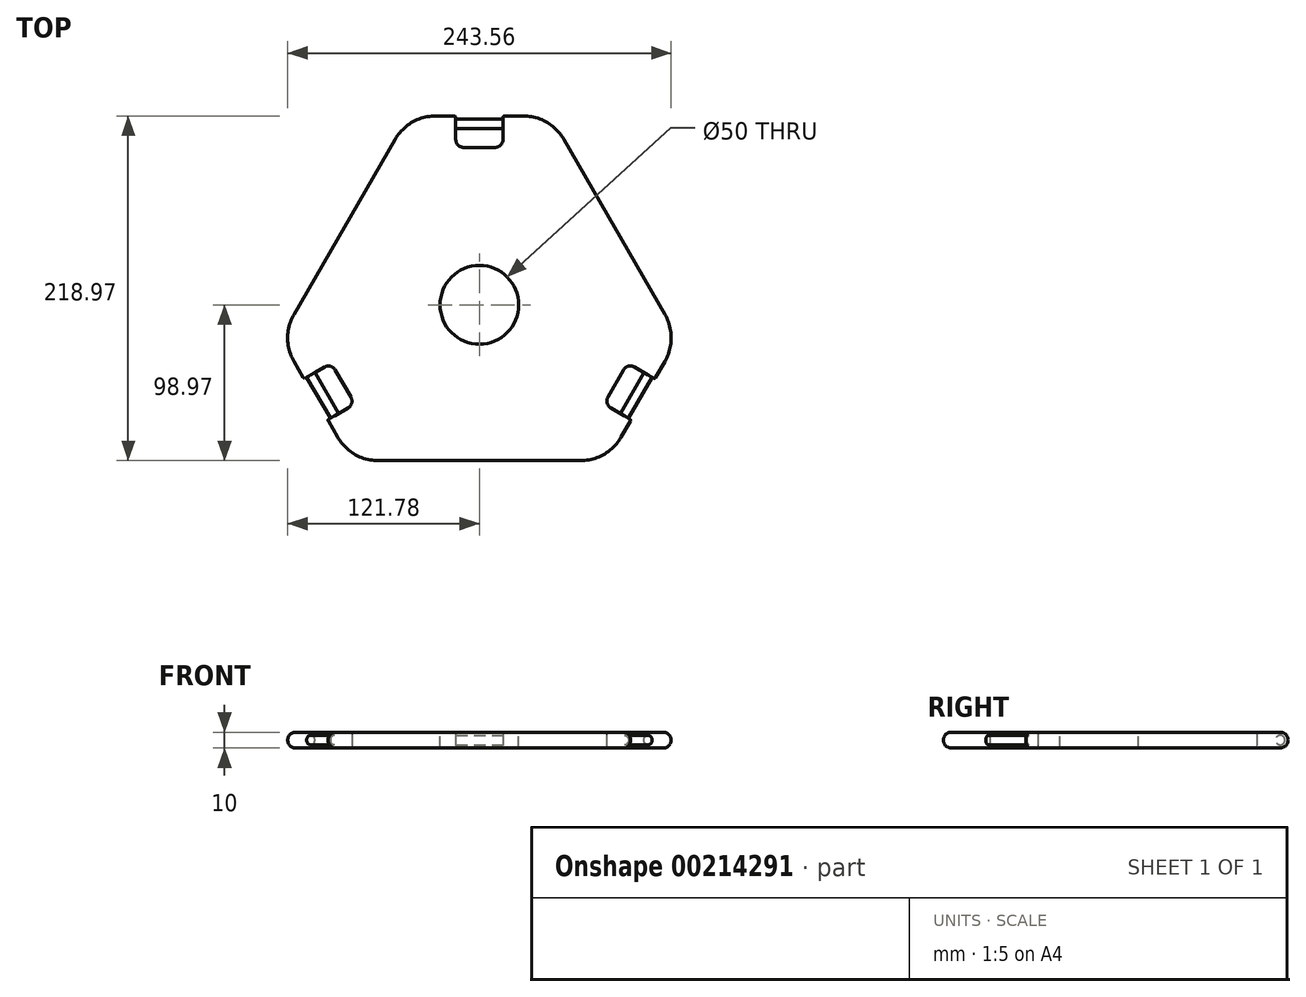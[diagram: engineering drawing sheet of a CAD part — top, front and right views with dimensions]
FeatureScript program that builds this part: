
annotation { "Feature Type Name" : "Feature", "Feature Type Description" : "" }
export const myFeature = defineFeature(function(context is Context, id is Id, definition is map)
    precondition{}
    {
        {
            var Q0;
            Q0=qCreatedBy(makeId("Top.planeOp"),FACE);
            var sketch = newSketch(context, id + "F0", { "sketchPlane" : qUnion([Q0])});
            skLineSegment(sketch, "E0", {"start": v(0, 100) * mm, "end": v(15, 100) * mm});
            skLineSegment(sketch, "E1", {"start": v(15, 100) * mm, "end": v(15, 120) * mm});
            skLineSegment(sketch, "E2", {"start": v(0, 0) * mm, "end": v(0, 100) * mm, "construction": true});
            skLineSegment(sketch, "E3.MirrorCS", {"start": v(0, 100) * mm, "end": v(-15, 100) * mm});
            skLineSegment(sketch, "E4.MirrorCS", {"start": v(-15, 100) * mm, "end": v(-15, 120) * mm});
            skLineSegment(sketch, "E5.1.0", {"start": v(-79.1, -63) * mm, "end": v(-96.42, -73) * mm});
            skLineSegment(sketch, "E5.1.1", {"start": v(-86.6, -50) * mm, "end": v(-79.1, -63) * mm});
            skLineSegment(sketch, "E5.1.2", {"start": v(-86.6, -50) * mm, "end": v(-94.1, -37) * mm});
            skLineSegment(sketch, "E5.1.3", {"start": v(-94.1, -37) * mm, "end": v(-111.42, -47) * mm});
            skLineSegment(sketch, "E5.2.0", {"start": v(94.1, -37) * mm, "end": v(111.42, -47) * mm});
            skLineSegment(sketch, "E5.2.1", {"start": v(86.6, -50) * mm, "end": v(94.1, -37) * mm});
            skLineSegment(sketch, "E5.2.2", {"start": v(86.6, -50) * mm, "end": v(79.1, -63) * mm});
            skLineSegment(sketch, "E5.2.3", {"start": v(79.1, -63) * mm, "end": v(96.42, -73) * mm});
            skPoint(sketch, "E5.center", {"position": v(0, 0) * mm});
            skLineSegment(sketch, "E6", {"start": v(15, 120) * mm, "end": v(45, 120) * mm});
            skLineSegment(sketch, "E7", {"start": v(45, 120) * mm, "end": v(126.42, -21.03) * mm});
            skLineSegment(sketch, "E8", {"start": v(126.42, -21.03) * mm, "end": v(111.42, -47) * mm});
            skLineSegment(sketch, "E9.1.0", {"start": v(-111.42, -47) * mm, "end": v(-126.42, -21.03) * mm});
            skLineSegment(sketch, "E9.1.1", {"start": v(-126.42, -21.03) * mm, "end": v(-45, 120) * mm});
            skLineSegment(sketch, "E9.1.2", {"start": v(-45, 120) * mm, "end": v(-15, 120) * mm});
            skLineSegment(sketch, "E9.2.0", {"start": v(96.42, -73) * mm, "end": v(81.42, -98.97) * mm});
            skLineSegment(sketch, "E9.2.1", {"start": v(81.42, -98.97) * mm, "end": v(-81.42, -98.97) * mm});
            skLineSegment(sketch, "E9.2.2", {"start": v(-81.42, -98.97) * mm, "end": v(-96.42, -73) * mm});
            skSolve(sketch);
        }
        {
            var Q0;
            Q0 = qSketchRegion(id + "F0", true);
            extrude(context, id + "F1", {"entities" : qUnion([Q0]), "depth" : 10 * mm});
        }
        {
            var Q0;
            Q0=makeQuery(id+"F1.opExtrude","SWEPT_EDGE",EDGE,{"disambiguationData":[OSD([sQuery(id+"F0.wireOp",EDGE,"E9.1.1"),sQuery(id+"F0.wireOp",EDGE,"E9.1.2")])]});
            var Q1;
            Q1=makeQuery(id+"F1.opExtrude","SWEPT_EDGE",EDGE,{"disambiguationData":[OSD([sQuery(id+"F0.wireOp",EDGE,"E6"),sQuery(id+"F0.wireOp",EDGE,"E7")])]});
            var Q2;
            Q2=makeQuery(id+"F1.opExtrude","SWEPT_EDGE",EDGE,{"disambiguationData":[OSD([sQuery(id+"F0.wireOp",EDGE,"E9.1.0"),sQuery(id+"F0.wireOp",EDGE,"E9.1.1")])]});
            var Q3;
            Q3=makeQuery(id+"F1.opExtrude","SWEPT_EDGE",EDGE,{"disambiguationData":[OSD([sQuery(id+"F0.wireOp",EDGE,"E7"),sQuery(id+"F0.wireOp",EDGE,"E8")])]});
            var Q4;
            Q4=makeQuery(id+"F1.opExtrude","SWEPT_EDGE",EDGE,{"disambiguationData":[OSD([sQuery(id+"F0.wireOp",EDGE,"E9.2.0"),sQuery(id+"F0.wireOp",EDGE,"E9.2.1")])]});
            var Q5;
            Q5=makeQuery(id+"F1.opExtrude","SWEPT_EDGE",EDGE,{"disambiguationData":[OSD([sQuery(id+"F0.wireOp",EDGE,"E9.2.1"),sQuery(id+"F0.wireOp",EDGE,"E9.2.2")])]});
            fillet(context, id + "F2", {"entities" : qUnion([Q0, Q1, Q2, Q3, Q4, Q5]), "radius" : 30 * mm, "tangentPropagation" : true, "allowEdgeOverflow" : false});
        }
        {
            var Q0;
            {var subQ0=sQuery(id+"F0.wireOp",EDGE,"E7");var subQ1=sQuery(id+"F0.wireOp",EDGE,"E6");Q0=makeQuery(id+"F2.opFillet","BLEND_EDGE",EDGE,{"blendedFrom":[makeQuery(id+"F1.opExtrude","SWEPT_EDGE",EDGE,{"disambiguationData":[OSD([subQ1,subQ0])]}),makeQuery(id+"F1.opExtrude","CAP_FACE",FACE,{"disambiguationData":[OSD([sQuery(id+"F0.wireOp",EDGE,"E0"),sQuery(id+"F0.wireOp",EDGE,"E1"),sQuery(id+"F0.wireOp",EDGE,"E3.MirrorCS"),sQuery(id+"F0.wireOp",EDGE,"E4.MirrorCS"),sQuery(id+"F0.wireOp",EDGE,"E5.1.0"),sQuery(id+"F0.wireOp",EDGE,"E5.1.1"),sQuery(id+"F0.wireOp",EDGE,"E5.1.2"),sQuery(id+"F0.wireOp",EDGE,"E5.1.3"),sQuery(id+"F0.wireOp",EDGE,"E5.2.0"),sQuery(id+"F0.wireOp",EDGE,"E5.2.1"),sQuery(id+"F0.wireOp",EDGE,"E5.2.2"),sQuery(id+"F0.wireOp",EDGE,"E5.2.3"),subQ1,subQ0,sQuery(id+"F0.wireOp",EDGE,"E8"),sQuery(id+"F0.wireOp",EDGE,"E9.1.0"),sQuery(id+"F0.wireOp",EDGE,"E9.1.1"),sQuery(id+"F0.wireOp",EDGE,"E9.1.2"),sQuery(id+"F0.wireOp",EDGE,"E9.2.0"),sQuery(id+"F0.wireOp",EDGE,"E9.2.1"),sQuery(id+"F0.wireOp",EDGE,"E9.2.2")])],"isStart":false})],"blendedInto":[makeQuery(id+"F1.opExtrude","CAP_FACE",FACE,{"disambiguationData":[OSD([sQuery(id+"F0.wireOp",EDGE,"E0"),sQuery(id+"F0.wireOp",EDGE,"E1"),sQuery(id+"F0.wireOp",EDGE,"E3.MirrorCS"),sQuery(id+"F0.wireOp",EDGE,"E4.MirrorCS"),sQuery(id+"F0.wireOp",EDGE,"E5.1.0"),sQuery(id+"F0.wireOp",EDGE,"E5.1.1"),sQuery(id+"F0.wireOp",EDGE,"E5.1.2"),sQuery(id+"F0.wireOp",EDGE,"E5.1.3"),sQuery(id+"F0.wireOp",EDGE,"E5.2.0"),sQuery(id+"F0.wireOp",EDGE,"E5.2.1"),sQuery(id+"F0.wireOp",EDGE,"E5.2.2"),sQuery(id+"F0.wireOp",EDGE,"E5.2.3"),subQ1,subQ0,sQuery(id+"F0.wireOp",EDGE,"E8"),sQuery(id+"F0.wireOp",EDGE,"E9.1.0"),sQuery(id+"F0.wireOp",EDGE,"E9.1.1"),sQuery(id+"F0.wireOp",EDGE,"E9.1.2"),sQuery(id+"F0.wireOp",EDGE,"E9.2.0"),sQuery(id+"F0.wireOp",EDGE,"E9.2.1"),sQuery(id+"F0.wireOp",EDGE,"E9.2.2")])],"isStart":false})]});}
            var Q1;
            {var subQ0=sQuery(id+"F0.wireOp",EDGE,"E9.2.1");var subQ1=sQuery(id+"F0.wireOp",EDGE,"E9.2.0");Q1=makeQuery(id+"F2.opFillet","BLEND_EDGE",EDGE,{"blendedFrom":[makeQuery(id+"F1.opExtrude","SWEPT_EDGE",EDGE,{"disambiguationData":[OSD([subQ1,subQ0])]}),makeQuery(id+"F1.opExtrude","CAP_FACE",FACE,{"disambiguationData":[OSD([sQuery(id+"F0.wireOp",EDGE,"E0"),sQuery(id+"F0.wireOp",EDGE,"E1"),sQuery(id+"F0.wireOp",EDGE,"E3.MirrorCS"),sQuery(id+"F0.wireOp",EDGE,"E4.MirrorCS"),sQuery(id+"F0.wireOp",EDGE,"E5.1.0"),sQuery(id+"F0.wireOp",EDGE,"E5.1.1"),sQuery(id+"F0.wireOp",EDGE,"E5.1.2"),sQuery(id+"F0.wireOp",EDGE,"E5.1.3"),sQuery(id+"F0.wireOp",EDGE,"E5.2.0"),sQuery(id+"F0.wireOp",EDGE,"E5.2.1"),sQuery(id+"F0.wireOp",EDGE,"E5.2.2"),sQuery(id+"F0.wireOp",EDGE,"E5.2.3"),sQuery(id+"F0.wireOp",EDGE,"E6"),sQuery(id+"F0.wireOp",EDGE,"E7"),sQuery(id+"F0.wireOp",EDGE,"E8"),sQuery(id+"F0.wireOp",EDGE,"E9.1.0"),sQuery(id+"F0.wireOp",EDGE,"E9.1.1"),sQuery(id+"F0.wireOp",EDGE,"E9.1.2"),subQ1,subQ0,sQuery(id+"F0.wireOp",EDGE,"E9.2.2")])],"isStart":false})],"blendedInto":[makeQuery(id+"F1.opExtrude","CAP_FACE",FACE,{"disambiguationData":[OSD([sQuery(id+"F0.wireOp",EDGE,"E0"),sQuery(id+"F0.wireOp",EDGE,"E1"),sQuery(id+"F0.wireOp",EDGE,"E3.MirrorCS"),sQuery(id+"F0.wireOp",EDGE,"E4.MirrorCS"),sQuery(id+"F0.wireOp",EDGE,"E5.1.0"),sQuery(id+"F0.wireOp",EDGE,"E5.1.1"),sQuery(id+"F0.wireOp",EDGE,"E5.1.2"),sQuery(id+"F0.wireOp",EDGE,"E5.1.3"),sQuery(id+"F0.wireOp",EDGE,"E5.2.0"),sQuery(id+"F0.wireOp",EDGE,"E5.2.1"),sQuery(id+"F0.wireOp",EDGE,"E5.2.2"),sQuery(id+"F0.wireOp",EDGE,"E5.2.3"),sQuery(id+"F0.wireOp",EDGE,"E6"),sQuery(id+"F0.wireOp",EDGE,"E7"),sQuery(id+"F0.wireOp",EDGE,"E8"),sQuery(id+"F0.wireOp",EDGE,"E9.1.0"),sQuery(id+"F0.wireOp",EDGE,"E9.1.1"),sQuery(id+"F0.wireOp",EDGE,"E9.1.2"),subQ1,subQ0,sQuery(id+"F0.wireOp",EDGE,"E9.2.2")])],"isStart":false})]});}
            var Q2;
            Q2=makeQuery(id+"F1.opExtrude","CAP_EDGE",EDGE,{"disambiguationData":[OSD([sQuery(id+"F0.wireOp",EDGE,"E9.1.1")])],"isStart":false});
            var Q3;
            {var subQ0=sQuery(id+"F0.wireOp",EDGE,"E9.2.1");var subQ1=sQuery(id+"F0.wireOp",EDGE,"E9.2.0");Q3=makeQuery(id+"F2.opFillet","BLEND_EDGE",EDGE,{"blendedFrom":[makeQuery(id+"F1.opExtrude","SWEPT_EDGE",EDGE,{"disambiguationData":[OSD([subQ1,subQ0])]}),makeQuery(id+"F1.opExtrude","CAP_FACE",FACE,{"disambiguationData":[OSD([sQuery(id+"F0.wireOp",EDGE,"E0"),sQuery(id+"F0.wireOp",EDGE,"E1"),sQuery(id+"F0.wireOp",EDGE,"E3.MirrorCS"),sQuery(id+"F0.wireOp",EDGE,"E4.MirrorCS"),sQuery(id+"F0.wireOp",EDGE,"E5.1.0"),sQuery(id+"F0.wireOp",EDGE,"E5.1.1"),sQuery(id+"F0.wireOp",EDGE,"E5.1.2"),sQuery(id+"F0.wireOp",EDGE,"E5.1.3"),sQuery(id+"F0.wireOp",EDGE,"E5.2.0"),sQuery(id+"F0.wireOp",EDGE,"E5.2.1"),sQuery(id+"F0.wireOp",EDGE,"E5.2.2"),sQuery(id+"F0.wireOp",EDGE,"E5.2.3"),sQuery(id+"F0.wireOp",EDGE,"E6"),sQuery(id+"F0.wireOp",EDGE,"E7"),sQuery(id+"F0.wireOp",EDGE,"E8"),sQuery(id+"F0.wireOp",EDGE,"E9.1.0"),sQuery(id+"F0.wireOp",EDGE,"E9.1.1"),sQuery(id+"F0.wireOp",EDGE,"E9.1.2"),subQ1,subQ0,sQuery(id+"F0.wireOp",EDGE,"E9.2.2")])],"isStart":true})],"blendedInto":[makeQuery(id+"F1.opExtrude","CAP_FACE",FACE,{"disambiguationData":[OSD([sQuery(id+"F0.wireOp",EDGE,"E0"),sQuery(id+"F0.wireOp",EDGE,"E1"),sQuery(id+"F0.wireOp",EDGE,"E3.MirrorCS"),sQuery(id+"F0.wireOp",EDGE,"E4.MirrorCS"),sQuery(id+"F0.wireOp",EDGE,"E5.1.0"),sQuery(id+"F0.wireOp",EDGE,"E5.1.1"),sQuery(id+"F0.wireOp",EDGE,"E5.1.2"),sQuery(id+"F0.wireOp",EDGE,"E5.1.3"),sQuery(id+"F0.wireOp",EDGE,"E5.2.0"),sQuery(id+"F0.wireOp",EDGE,"E5.2.1"),sQuery(id+"F0.wireOp",EDGE,"E5.2.2"),sQuery(id+"F0.wireOp",EDGE,"E5.2.3"),sQuery(id+"F0.wireOp",EDGE,"E6"),sQuery(id+"F0.wireOp",EDGE,"E7"),sQuery(id+"F0.wireOp",EDGE,"E8"),sQuery(id+"F0.wireOp",EDGE,"E9.1.0"),sQuery(id+"F0.wireOp",EDGE,"E9.1.1"),sQuery(id+"F0.wireOp",EDGE,"E9.1.2"),subQ1,subQ0,sQuery(id+"F0.wireOp",EDGE,"E9.2.2")])],"isStart":true})]});}
            var Q4;
            {var subQ0=sQuery(id+"F0.wireOp",EDGE,"E8");var subQ1=sQuery(id+"F0.wireOp",EDGE,"E7");Q4=makeQuery(id+"F2.opFillet","BLEND_EDGE",EDGE,{"blendedFrom":[makeQuery(id+"F1.opExtrude","SWEPT_EDGE",EDGE,{"disambiguationData":[OSD([subQ1,subQ0])]}),makeQuery(id+"F1.opExtrude","CAP_FACE",FACE,{"disambiguationData":[OSD([sQuery(id+"F0.wireOp",EDGE,"E0"),sQuery(id+"F0.wireOp",EDGE,"E1"),sQuery(id+"F0.wireOp",EDGE,"E3.MirrorCS"),sQuery(id+"F0.wireOp",EDGE,"E4.MirrorCS"),sQuery(id+"F0.wireOp",EDGE,"E5.1.0"),sQuery(id+"F0.wireOp",EDGE,"E5.1.1"),sQuery(id+"F0.wireOp",EDGE,"E5.1.2"),sQuery(id+"F0.wireOp",EDGE,"E5.1.3"),sQuery(id+"F0.wireOp",EDGE,"E5.2.0"),sQuery(id+"F0.wireOp",EDGE,"E5.2.1"),sQuery(id+"F0.wireOp",EDGE,"E5.2.2"),sQuery(id+"F0.wireOp",EDGE,"E5.2.3"),sQuery(id+"F0.wireOp",EDGE,"E6"),subQ1,subQ0,sQuery(id+"F0.wireOp",EDGE,"E9.1.0"),sQuery(id+"F0.wireOp",EDGE,"E9.1.1"),sQuery(id+"F0.wireOp",EDGE,"E9.1.2"),sQuery(id+"F0.wireOp",EDGE,"E9.2.0"),sQuery(id+"F0.wireOp",EDGE,"E9.2.1"),sQuery(id+"F0.wireOp",EDGE,"E9.2.2")])],"isStart":true})],"blendedInto":[makeQuery(id+"F1.opExtrude","CAP_FACE",FACE,{"disambiguationData":[OSD([sQuery(id+"F0.wireOp",EDGE,"E0"),sQuery(id+"F0.wireOp",EDGE,"E1"),sQuery(id+"F0.wireOp",EDGE,"E3.MirrorCS"),sQuery(id+"F0.wireOp",EDGE,"E4.MirrorCS"),sQuery(id+"F0.wireOp",EDGE,"E5.1.0"),sQuery(id+"F0.wireOp",EDGE,"E5.1.1"),sQuery(id+"F0.wireOp",EDGE,"E5.1.2"),sQuery(id+"F0.wireOp",EDGE,"E5.1.3"),sQuery(id+"F0.wireOp",EDGE,"E5.2.0"),sQuery(id+"F0.wireOp",EDGE,"E5.2.1"),sQuery(id+"F0.wireOp",EDGE,"E5.2.2"),sQuery(id+"F0.wireOp",EDGE,"E5.2.3"),sQuery(id+"F0.wireOp",EDGE,"E6"),subQ1,subQ0,sQuery(id+"F0.wireOp",EDGE,"E9.1.0"),sQuery(id+"F0.wireOp",EDGE,"E9.1.1"),sQuery(id+"F0.wireOp",EDGE,"E9.1.2"),sQuery(id+"F0.wireOp",EDGE,"E9.2.0"),sQuery(id+"F0.wireOp",EDGE,"E9.2.1"),sQuery(id+"F0.wireOp",EDGE,"E9.2.2")])],"isStart":true})]});}
            var Q5;
            {var subQ0=sQuery(id+"F0.wireOp",EDGE,"E9.1.1");var subQ1=sQuery(id+"F0.wireOp",EDGE,"E9.1.0");Q5=makeQuery(id+"F2.opFillet","BLEND_EDGE",EDGE,{"blendedFrom":[makeQuery(id+"F1.opExtrude","SWEPT_EDGE",EDGE,{"disambiguationData":[OSD([subQ1,subQ0])]}),makeQuery(id+"F1.opExtrude","CAP_FACE",FACE,{"disambiguationData":[OSD([sQuery(id+"F0.wireOp",EDGE,"E0"),sQuery(id+"F0.wireOp",EDGE,"E1"),sQuery(id+"F0.wireOp",EDGE,"E3.MirrorCS"),sQuery(id+"F0.wireOp",EDGE,"E4.MirrorCS"),sQuery(id+"F0.wireOp",EDGE,"E5.1.0"),sQuery(id+"F0.wireOp",EDGE,"E5.1.1"),sQuery(id+"F0.wireOp",EDGE,"E5.1.2"),sQuery(id+"F0.wireOp",EDGE,"E5.1.3"),sQuery(id+"F0.wireOp",EDGE,"E5.2.0"),sQuery(id+"F0.wireOp",EDGE,"E5.2.1"),sQuery(id+"F0.wireOp",EDGE,"E5.2.2"),sQuery(id+"F0.wireOp",EDGE,"E5.2.3"),sQuery(id+"F0.wireOp",EDGE,"E6"),sQuery(id+"F0.wireOp",EDGE,"E7"),sQuery(id+"F0.wireOp",EDGE,"E8"),subQ1,subQ0,sQuery(id+"F0.wireOp",EDGE,"E9.1.2"),sQuery(id+"F0.wireOp",EDGE,"E9.2.0"),sQuery(id+"F0.wireOp",EDGE,"E9.2.1"),sQuery(id+"F0.wireOp",EDGE,"E9.2.2")])],"isStart":true})],"blendedInto":[makeQuery(id+"F1.opExtrude","CAP_FACE",FACE,{"disambiguationData":[OSD([sQuery(id+"F0.wireOp",EDGE,"E0"),sQuery(id+"F0.wireOp",EDGE,"E1"),sQuery(id+"F0.wireOp",EDGE,"E3.MirrorCS"),sQuery(id+"F0.wireOp",EDGE,"E4.MirrorCS"),sQuery(id+"F0.wireOp",EDGE,"E5.1.0"),sQuery(id+"F0.wireOp",EDGE,"E5.1.1"),sQuery(id+"F0.wireOp",EDGE,"E5.1.2"),sQuery(id+"F0.wireOp",EDGE,"E5.1.3"),sQuery(id+"F0.wireOp",EDGE,"E5.2.0"),sQuery(id+"F0.wireOp",EDGE,"E5.2.1"),sQuery(id+"F0.wireOp",EDGE,"E5.2.2"),sQuery(id+"F0.wireOp",EDGE,"E5.2.3"),sQuery(id+"F0.wireOp",EDGE,"E6"),sQuery(id+"F0.wireOp",EDGE,"E7"),sQuery(id+"F0.wireOp",EDGE,"E8"),subQ1,subQ0,sQuery(id+"F0.wireOp",EDGE,"E9.1.2"),sQuery(id+"F0.wireOp",EDGE,"E9.2.0"),sQuery(id+"F0.wireOp",EDGE,"E9.2.1"),sQuery(id+"F0.wireOp",EDGE,"E9.2.2")])],"isStart":true})]});}
            fillet(context, id + "F3", {"entities" : qUnion([Q0, Q1, Q2, Q3, Q4, Q5]), "radius" : 5 * mm, "tangentPropagation" : true, "allowEdgeOverflow" : false});
        }
        {
            var Q0;
            Q0=qCreatedBy(makeId("Right.planeOp"),FACE);
            var sketch = newSketch(context, id + "F4", { "sketchPlane" : qUnion([Q0])});
            skLineSegment(sketch, "E10", {"start": v(0, 0) * mm, "end": v(0, 47.73) * mm});
            skSolve(sketch);
        }
        {
            var Q0;
            Q0=makeQuery(id+"F1.opExtrude","SWEPT_FACE",FACE,{"disambiguationData":[OSD([sQuery(id+"F0.wireOp",EDGE,"E1")])]});
            var sketch = newSketch(context, id + "F5", { "sketchPlane" : qUnion([Q0])});
            skCircle(sketch, "E11", {"center": v(-115, 5) * mm, "radius": 3 * mm});
            skSolve(sketch);
        }
        {
            var Q0;
            Q0 = qSketchRegion(id + "F5", true);
            var Q1;
            Q1=makeQuery(id+"F1.opExtrude","SWEPT_FACE",FACE,{"disambiguationData":[OSD([sQuery(id+"F0.wireOp",EDGE,"E4.MirrorCS")])]});
            extrude(context, id + "F6", {"entities" : qUnion([Q0]), "endBound" : BoundingType.UP_TO_SURFACE, "endBoundEntityFace" : qUnion([Q1]), "depth" : 25 * mm});
        }
        {
            var Q0;
            Q0=makeQuery(id+"F6.opExtrude","SWEPT_BODY",BODY,{"disambiguationData":[OSD([sQuery(id+"F5.wireOp",EDGE,"E11")])]});
            var Q1;
            Q1=sQuery(id+"F4.wireOp",EDGE,"E10");
            circularPattern(context, id + "F7", {"entities" : qUnion([Q0]), "axis" : qUnion([Q1]), "angle" : 360 * degree, "instanceCount" : 3, "equalSpace" : true});
        }
        {
            var Q0;
            Q0=makeQuery(id+"F1.opExtrude","SWEPT_EDGE",EDGE,{"disambiguationData":[OSD([sQuery(id+"F0.wireOp",EDGE,"E5.1.0"),sQuery(id+"F0.wireOp",EDGE,"E5.1.1")])]});
            var Q1;
            Q1=makeQuery(id+"F1.opExtrude","SWEPT_EDGE",EDGE,{"disambiguationData":[OSD([sQuery(id+"F0.wireOp",EDGE,"E5.1.2"),sQuery(id+"F0.wireOp",EDGE,"E5.1.3")])]});
            var Q2;
            Q2=makeQuery(id+"F1.opExtrude","SWEPT_EDGE",EDGE,{"disambiguationData":[OSD([sQuery(id+"F0.wireOp",EDGE,"E5.2.0"),sQuery(id+"F0.wireOp",EDGE,"E5.2.1")])]});
            var Q3;
            Q3=makeQuery(id+"F1.opExtrude","SWEPT_EDGE",EDGE,{"disambiguationData":[OSD([sQuery(id+"F0.wireOp",EDGE,"E5.2.2"),sQuery(id+"F0.wireOp",EDGE,"E5.2.3")])]});
            var Q4;
            Q4=makeQuery(id+"F1.opExtrude","SWEPT_EDGE",EDGE,{"disambiguationData":[OSD([sQuery(id+"F0.wireOp",EDGE,"E3.MirrorCS"),sQuery(id+"F0.wireOp",EDGE,"E4.MirrorCS")])]});
            var Q5;
            Q5=makeQuery(id+"F1.opExtrude","SWEPT_EDGE",EDGE,{"disambiguationData":[OSD([sQuery(id+"F0.wireOp",EDGE,"E0"),sQuery(id+"F0.wireOp",EDGE,"E1")])]});
            fillet(context, id + "F8", {"entities" : qUnion([Q0, Q1, Q2, Q3, Q4, Q5]), "radius" : 5 * mm, "tangentPropagation" : true, "allowEdgeOverflow" : false});
        }
        {
            var Q0;
            Q0=makeQuery(id+"F1.opExtrude","CAP_EDGE",EDGE,{"disambiguationData":[OSD([sQuery(id+"F0.wireOp",EDGE,"E5.1.3")])],"isStart":true});
            var Q1;
            Q1=makeQuery(id+"F1.opExtrude","CAP_EDGE",EDGE,{"disambiguationData":[OSD([sQuery(id+"F0.wireOp",EDGE,"E4.MirrorCS")])],"isStart":true});
            var Q2;
            Q2=makeQuery(id+"F1.opExtrude","CAP_EDGE",EDGE,{"disambiguationData":[OSD([sQuery(id+"F0.wireOp",EDGE,"E5.2.1"),sQuery(id+"F0.wireOp",EDGE,"E5.2.2")])],"isStart":true});
            fillet(context, id + "F9", {"entities" : qUnion([Q0, Q1, Q2]), "radius" : 1 * mm, "tangentPropagation" : true, "allowEdgeOverflow" : false});
        }
        {
            var Q0;
            Q0=makeQuery(id+"F1.opExtrude","CAP_FACE",FACE,{"disambiguationData":[OSD([sQuery(id+"F0.wireOp",EDGE,"E0"),sQuery(id+"F0.wireOp",EDGE,"E1"),sQuery(id+"F0.wireOp",EDGE,"E3.MirrorCS"),sQuery(id+"F0.wireOp",EDGE,"E4.MirrorCS"),sQuery(id+"F0.wireOp",EDGE,"E5.1.0"),sQuery(id+"F0.wireOp",EDGE,"E5.1.1"),sQuery(id+"F0.wireOp",EDGE,"E5.1.2"),sQuery(id+"F0.wireOp",EDGE,"E5.1.3"),sQuery(id+"F0.wireOp",EDGE,"E5.2.0"),sQuery(id+"F0.wireOp",EDGE,"E5.2.1"),sQuery(id+"F0.wireOp",EDGE,"E5.2.2"),sQuery(id+"F0.wireOp",EDGE,"E5.2.3"),sQuery(id+"F0.wireOp",EDGE,"E6"),sQuery(id+"F0.wireOp",EDGE,"E7"),sQuery(id+"F0.wireOp",EDGE,"E8"),sQuery(id+"F0.wireOp",EDGE,"E9.1.0"),sQuery(id+"F0.wireOp",EDGE,"E9.1.1"),sQuery(id+"F0.wireOp",EDGE,"E9.1.2"),sQuery(id+"F0.wireOp",EDGE,"E9.2.0"),sQuery(id+"F0.wireOp",EDGE,"E9.2.1"),sQuery(id+"F0.wireOp",EDGE,"E9.2.2")])],"isStart":false});
            var sketch = newSketch(context, id + "F10", { "sketchPlane" : qUnion([Q0])});
            skCircle(sketch, "E12", {"center": v(0, 0) * mm, "radius": 25 * mm});
            skSolve(sketch);
        }
        {
            var Q0;
            Q0=makeQuery(id+"F10.imprint","IMPRINT",FACE,{"disambiguationData":[TD([[makeQuery(id+"F10.imprint","IMPRINT",EDGE,{"derivedFrom":sQuery(id+"F10.wireOp",EDGE,"E12")}),1.0]])]});
            extrude(context, id + "F11", {"entities" : qUnion([Q0]), "operationType" : NewBodyOperationType.REMOVE, "oppositeDirection" : true, "depth" : 25 * mm});
        }
    });
